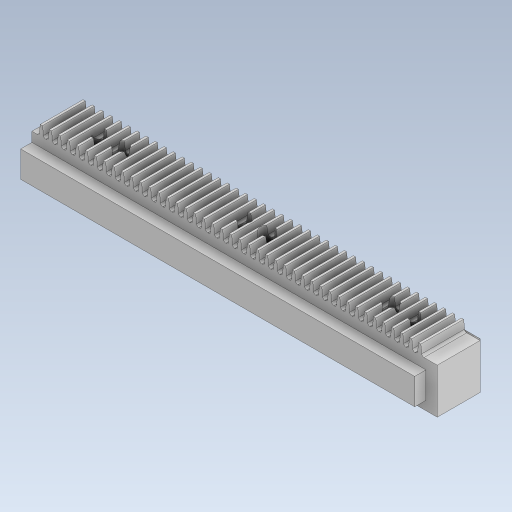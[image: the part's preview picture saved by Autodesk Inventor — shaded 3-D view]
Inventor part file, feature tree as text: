
AUTODESK INVENTOR PART (.ipt)
format: ipt  version: 2023.5 (Build 275446000, 446)  size: 1,240,064 bytes
history: native  units: in
note: dims shown in document units (in); Inventor stores cm internally (conversion verified against a paired STEP export)
features: extrude x9, sketch x8, plane x2, fillet x1, pattern_linear x1
ambient origin geometry x8: Origin, YZ Plane, XZ Plane, XY Plane, X Axis, Y Axis, Z Axis, Center Point
bodies: Solid1 (feature_tree)
feature tree (21):
  sketch  "Sketch1"  dims[d0=3.937in d1=0.748in]
  extrude  "Extrusion1"  Depth=0.748in
  extrude  "Extrusion2"  Depth=0.1969in
  extrude  "Extrusion3"  Depth=0.1969in
  plane  "Work Plane1"
  extrude  "Extrusion5"  Depth=0.4606in
  fillet  "Fillet1"  Radius=0.1969in
  extrude  "Extrusion7"  Depth=0.1969in TaperAngle=0.0deg
  extrude  "Extrusion9"  Depth=0.0394in
  pattern_linear  "Rectangular Pattern2"  Spacing1=0.0394in  [1 undecoded]
  extrude  "Extrusion10"  Depth=0.1181in TaperAngle=0.0deg
  plane  "Work Plane3"
  extrude  "Extrusion11"  Depth=0.1181in TaperAngle=0.0deg
  extrude  "Extrusion12"  Depth=0.1181in
  sketch  "Sketch3"  dims[d2=0.1969in d3=0.1969in]
  sketch  "Sketch4"  dims[d4=0.1969in d5=0.1969in]
  sketch  "Sketch7"  dims[d6=0.7874in d7=0.0in d8=0.4606in d9=0.1969in d10=0.0in]
  sketch  "Sketch10"  dims[d11=0.4606in d12=0.1969in d13=0.0in]
  sketch  "Sketch11"  dims[d27=3.7402in d28=0.0394in]
  sketch  "Sketch12"  dims[d29=0.0748in]
  sketch  "Sketch13"  dims[d30=0.374in d31=0.374in d32=0.0in d33=0.0in d34=0.0394in d45=0.7874in d46=0.0in d55=3.1496in d56=0.0in d57=16.9291in d59=0.1575in d60=0.1181in d61=0.7874in d62=0.1181in d63=0.3937in d64=0.1181in d65=0.7874in d66=0.1181in d67=0.3937in d68=0.1181in d69=0.1969in d70=1.1811in d71=0.0in d72=0.2362in d73=0.2362in d74=0.2362in d75=0.2362in d76=0.2362in d77=0.1969in d78=0.5906in d79=0.0in d80=0.1969in d81=0.0in]
note: 1 required parameter value undecoded (feature->parameter linkage not recoverable at this tier; creation-order binding heuristic only, values carry confidence <= 0.55)
